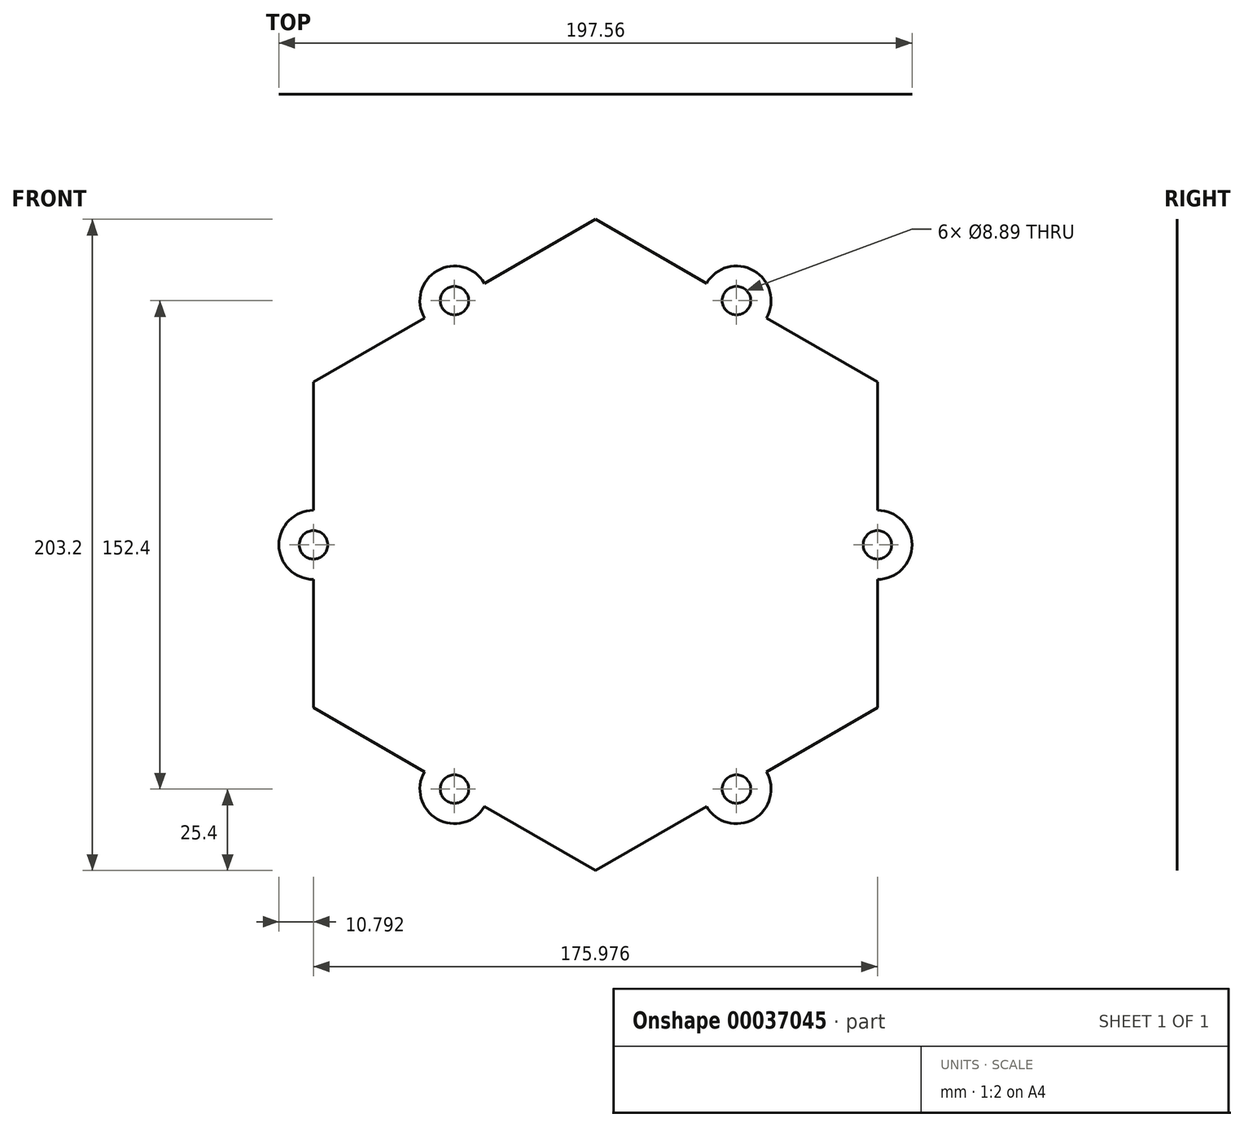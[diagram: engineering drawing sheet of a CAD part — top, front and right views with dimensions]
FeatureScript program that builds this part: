
annotation { "Feature Type Name" : "Feature", "Feature Type Description" : "" }
export const myFeature = defineFeature(function(context is Context, id is Id, definition is map)
    precondition{}
    {
        {
            var Q0;
            Q0=qCreatedBy(makeId("Front.planeOp"),FACE);
            var sketch = newSketch(context, id + "F0", { "sketchPlane" : qUnion([Q0])});
            skCircle(sketch, "E0.cCircle", {"center": v(0, 0) * mm, "radius": 87.99 * mm, "construction": true});
            skLineSegment(sketch, "E0.0", {"start": v(0, 101.6) * mm, "end": v(87.99, 50.8) * mm});
            skLineSegment(sketch, "E0.1", {"start": v(87.99, 50.8) * mm, "end": v(87.99, -50.8) * mm});
            skLineSegment(sketch, "E0.2", {"start": v(87.99, -50.8) * mm, "end": v(0, -101.6) * mm});
            skLineSegment(sketch, "E0.3", {"start": v(0, -101.6) * mm, "end": v(-87.99, -50.8) * mm});
            skLineSegment(sketch, "E0.4", {"start": v(-87.99, -50.8) * mm, "end": v(-87.99, 50.8) * mm});
            skLineSegment(sketch, "E0.5", {"start": v(-87.99, 50.8) * mm, "end": v(0, 101.6) * mm});
            skPoint(sketch, "E0.0.midPoint", {"position": v(44, 76.2) * mm});
            skSolve(sketch);
        }
        {
            var Q0;
            Q0=qSketchRegion(id+"F0",true);
            extrude(context, id + "F1", {"entities" : qUnion([Q0]), "depth" : 1 / 203.2 * mm});
        }
        {
            var Q0;
            Q0=makeQuery(id+"F1.opExtrude","CAP_FACE",FACE,{"disambiguationData":[OSD([sQuery(id+"F0.wireOp",EDGE,"E0.0"),sQuery(id+"F0.wireOp",EDGE,"E0.1"),sQuery(id+"F0.wireOp",EDGE,"E0.2"),sQuery(id+"F0.wireOp",EDGE,"E0.3"),sQuery(id+"F0.wireOp",EDGE,"E0.4"),sQuery(id+"F0.wireOp",EDGE,"E0.5")])],"isStart":false});
            var sketch = newSketch(context, id + "F2", { "sketchPlane" : qUnion([Q0])});
            skSolve(sketch);
        }
        {
            var Q0;
            Q0=qCreatedBy(makeId("Front.planeOp"),FACE);
            var sketch = newSketch(context, id + "F3", { "sketchPlane" : qUnion([Q0])});
            skLineSegment(sketch, "E1.left", {"start": v(87.99, 10.8) * mm, "end": v(87.99, -10.8) * mm});
            skPoint(sketch, "E2", {"position": v(87.99, 0) * mm});
            skPoint(sketch, "E3", {"position": v(96.67, 0) * mm});
            skArc(sketch, "E4", {"start": v(87.99, -10.8) * mm, "mid": v(98.78, 0) * mm, "end": v(87.99, 10.8) * mm});
            skArc(sketch, "E5.1.0", {"start": v(53.34, 70.8) * mm, "mid": v(49.4, 85.55) * mm, "end": v(34.65, 81.6) * mm});
            skArc(sketch, "E5.2.0", {"start": v(-34.65, 81.6) * mm, "mid": v(-49.4, 85.55) * mm, "end": v(-53.34, 70.8) * mm});
            skArc(sketch, "E5.3.0", {"start": v(-87.99, 10.8) * mm, "mid": v(-98.78, 0) * mm, "end": v(-87.99, -10.8) * mm});
            skArc(sketch, "E5.4.0", {"start": v(-53.34, -70.8) * mm, "mid": v(-49.4, -85.55) * mm, "end": v(-34.65, -81.6) * mm});
            skArc(sketch, "E5.5.0", {"start": v(34.65, -81.6) * mm, "mid": v(49.4, -85.55) * mm, "end": v(53.34, -70.8) * mm});
            skPoint(sketch, "E5.center", {"position": v(0, 0) * mm});
            skLineSegment(sketch, "E6", {"start": v(34.65, 81.6) * mm, "end": v(53.34, 70.8) * mm});
            skLineSegment(sketch, "E7", {"start": v(-34.65, 81.6) * mm, "end": v(-53.34, 70.8) * mm});
            skLineSegment(sketch, "E8", {"start": v(-87.99, 10.8) * mm, "end": v(-87.99, -10.8) * mm});
            skLineSegment(sketch, "E9", {"start": v(-53.34, -70.8) * mm, "end": v(-34.65, -81.6) * mm});
            skLineSegment(sketch, "E10", {"start": v(34.65, -81.6) * mm, "end": v(53.34, -70.8) * mm});
            skSolve(sketch);
        }
        {
            var Q0;
            Q0 = qSketchRegion(id + "F3", true);
            extrude(context, id + "F4", {"entities" : qUnion([Q0]), "operationType" : NewBodyOperationType.ADD, "depth" : 1 / 203.2 * mm});
        }
        {
            var Q0;
            Q0=makeQuery(id+"F2.imprint","IMPRINT",FACE,{"disambiguationData":[TD([[makeQuery(id+"F2.imprint","IMPRINT",EDGE,{"derivedFrom":makeQuery(id+"F1.opExtrude","CAP_EDGE",EDGE,{"disambiguationData":[OSD([sQuery(id+"F0.wireOp",EDGE,"E0.0")])],"isStart":false})}),-1.0]])]});
            var sketch = newSketch(context, id + "F5", { "sketchPlane" : qUnion([Q0])});
            skCircle(sketch, "E11", {"center": v(44, 76.2) * mm, "radius": 4.45 * mm});
            skCircle(sketch, "E12.1.0", {"center": v(-44, 76.2) * mm, "radius": 4.45 * mm});
            skCircle(sketch, "E12.2.0", {"center": v(-87.99, 0) * mm, "radius": 4.45 * mm});
            skCircle(sketch, "E12.3.0", {"center": v(-44, -76.2) * mm, "radius": 4.45 * mm});
            skCircle(sketch, "E12.4.0", {"center": v(44, -76.2) * mm, "radius": 4.45 * mm});
            skCircle(sketch, "E12.5.0", {"center": v(87.99, 0) * mm, "radius": 4.45 * mm});
            skPoint(sketch, "E12.center", {"position": v(0, 0) * mm});
            skSolve(sketch);
        }
        {
            var Q0;
            Q0 = qSketchRegion(id + "F5", true);
            extrude(context, id + "F6", {"entities" : qUnion([Q0]), "operationType" : NewBodyOperationType.REMOVE, "endBound" : BoundingType.THROUGH_ALL, "oppositeDirection" : true, "depth" : 25.4 * mm});
        }
    });
